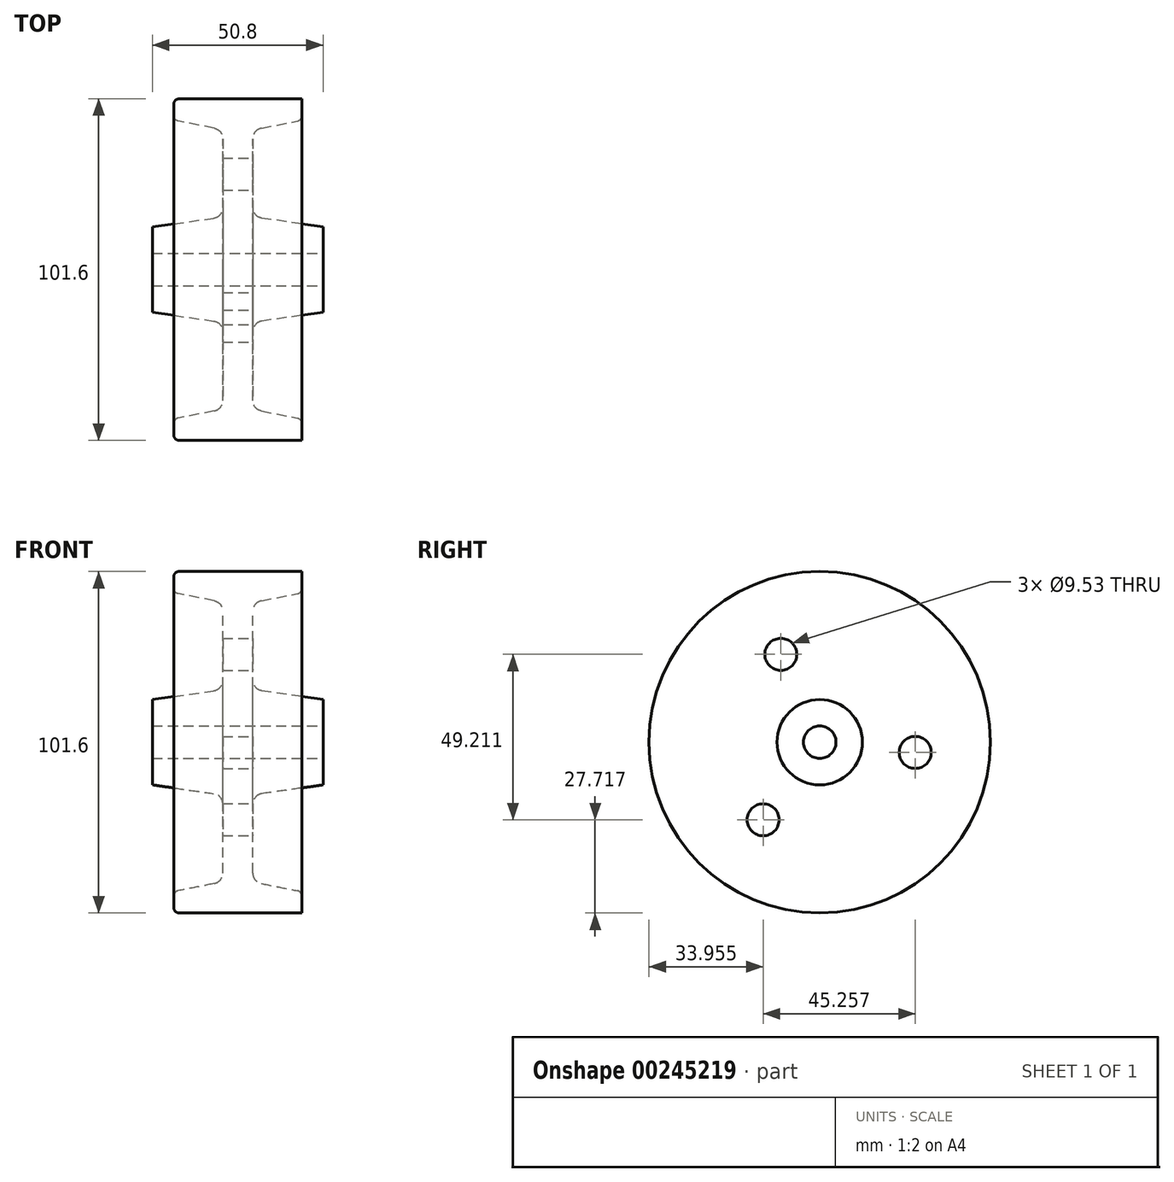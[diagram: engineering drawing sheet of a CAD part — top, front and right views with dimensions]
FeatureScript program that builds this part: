
annotation { "Feature Type Name" : "Feature", "Feature Type Description" : "" }
export const myFeature = defineFeature(function(context is Context, id is Id, definition is map)
    precondition{}
    {
        {
            var Q0;
            Q0=qCreatedBy(makeId("Front.planeOp"),FACE);
            var sketch = newSketch(context, id + "F0", { "sketchPlane" : qUnion([Q0])});
            skLineSegment(sketch, "E0", {"start": v(-43.53, 27.61) * mm, "end": v(7.27, 27.61) * mm});
            skLineSegment(sketch, "E1", {"start": v(7.27, 27.61) * mm, "end": v(7.27, 19.74) * mm});
            skLineSegment(sketch, "E2", {"start": v(-43.53, 27.61) * mm, "end": v(-43.53, 19.74) * mm});
            skLineSegment(sketch, "E3", {"start": v(-18.13, 27.61) * mm, "end": v(-18.13, -18.36) * mm});
            skLineSegment(sketch, "E4", {"start": v(-18.13, -18.36) * mm, "end": v(-35.59, -18.36) * mm});
            skLineSegment(sketch, "E5", {"start": v(-18.13, -18.36) * mm, "end": v(0.92, -18.36) * mm});
            skLineSegment(sketch, "E6", {"start": v(-37.18, -18.36) * mm, "end": v(-37.18, -12.01) * mm});
            skLineSegment(sketch, "E7", {"start": v(-37.18, -16.77) * mm, "end": v(-37.18, -13.31) * mm});
            skLineSegment(sketch, "E8", {"start": v(-25.13, -9.6) * mm, "end": v(-35.9, -11.76) * mm});
            skPoint(sketch, "E9.orphan", {"position": v(-37.18, -9.1) * mm});
            skLineSegment(sketch, "E10", {"start": v(-25.3, 17.14) * mm, "end": v(-43.53, 19.74) * mm});
            skLineSegment(sketch, "E11.MirrorCS", {"start": v(0.92, -16.77) * mm, "end": v(0.92, -13.31) * mm});
            skLineSegment(sketch, "E12.MirrorCS", {"start": v(-18.13, -18.36) * mm, "end": v(-0.66, -18.36) * mm});
            skLineSegment(sketch, "E13.MirrorCS", {"start": v(0.92, -18.36) * mm, "end": v(0.92, -12.01) * mm});
            skLineSegment(sketch, "E14.MirrorCS", {"start": v(-11.12, -9.6) * mm, "end": v(-0.35, -11.76) * mm});
            skLineSegment(sketch, "E15.MirrorCS", {"start": v(-10.95, 17.14) * mm, "end": v(7.27, 19.74) * mm});
            skPoint(sketch, "E16.MirrorP", {"position": v(0.92, -9.1) * mm});
            skPoint(sketch, "E17.end.orphan", {"position": v(-21.3, -10.7) * mm});
            skPoint(sketch, "E18.MirrorCS.end.orphan", {"position": v(-14.95, -6.4) * mm});
            skPoint(sketch, "E18.MirrorCS.start.orphan", {"position": v(-18.13, -5.1) * mm});
            skPoint(sketch, "E19.end.orphan", {"position": v(-21.3, -6.4) * mm});
            skPoint(sketch, "E20.MirrorCS.end.orphan", {"position": v(-14.95, -10.7) * mm});
            skPoint(sketch, "E21.orphan", {"position": v(-21.3, 27.61) * mm});
            skPoint(sketch, "E22.orphan", {"position": v(-14.95, 27.61) * mm});
            skLineSegment(sketch, "E23.trimOffspring", {"start": v(-22.58, -6.49) * mm, "end": v(-22.58, 14) * mm});
            skLineSegment(sketch, "E24.trimOffspring", {"start": v(-13.68, -6.49) * mm, "end": v(-13.68, 14) * mm});
            skPoint(sketch, "E25.MirrorCS.start.orphan", {"position": v(-14.95, -18.36) * mm});
            skPoint(sketch, "E26.start.orphan", {"position": v(-21.3, -18.36) * mm});
            skPoint(sketch, "E27.visualSharp", {"position": v(-22.58, -9.1) * mm});
            skArc(sketch, "E27.filletArc", {"start": v(-25.13, -9.6) * mm, "mid": v(-23.3, -8.5) * mm, "end": v(-22.58, -6.49) * mm});
            skPoint(sketch, "E28.visualSharp", {"position": v(-13.68, -9.1) * mm});
            skArc(sketch, "E28.filletArc", {"start": v(-13.68, -6.49) * mm, "mid": v(-12.96, -8.5) * mm, "end": v(-11.12, -9.6) * mm});
            skPoint(sketch, "E29.visualSharp", {"position": v(-22.58, 16.75) * mm});
            skArc(sketch, "E29.filletArc", {"start": v(-22.58, 14) * mm, "mid": v(-23.35, 16.07) * mm, "end": v(-25.3, 17.14) * mm});
            skPoint(sketch, "E30.visualSharp", {"position": v(-13.68, 16.75) * mm});
            skArc(sketch, "E30.filletArc", {"start": v(-10.95, 17.14) * mm, "mid": v(-12.9, 16.07) * mm, "end": v(-13.68, 14) * mm});
            skPoint(sketch, "E31.visualSharp", {"position": v(-37.18, -12.01) * mm});
            skArc(sketch, "E31.filletArc", {"start": v(-35.9, -11.76) * mm, "mid": v(-36.82, -12.3) * mm, "end": v(-37.18, -13.31) * mm});
            skPoint(sketch, "E32.visualSharp", {"position": v(0.92, -12.01) * mm});
            skArc(sketch, "E32.filletArc", {"start": v(0.92, -13.31) * mm, "mid": v(0.56, -12.3) * mm, "end": v(-0.35, -11.76) * mm});
            skPoint(sketch, "E33.visualSharp", {"position": v(0.92, -18.36) * mm});
            skArc(sketch, "E33.filletArc", {"start": v(-0.66, -18.36) * mm, "mid": v(0.46, -17.9) * mm, "end": v(0.92, -16.77) * mm});
            skPoint(sketch, "E34.visualSharp", {"position": v(-37.18, -18.36) * mm});
            skArc(sketch, "E34.filletArc", {"start": v(-37.18, -16.77) * mm, "mid": v(-36.71, -17.9) * mm, "end": v(-35.59, -18.36) * mm});
            skPoint(sketch, "E35.end.orphan", {"position": v(-18.13, 32.44) * mm});
            skLineSegment(sketch, "E36", {"start": v(9.17, 32.44) * mm, "end": v(-45.24, 32.44) * mm});
            skSolve(sketch);
        }
        {
            var Q0;
            {var subQ1=sQuery(id+"F0.wireOp",EDGE,"E2");Q0=makeQuery(id+"F0.imprint","IMPRINT",FACE,{"disambiguationData":[TD([[makeQuery(id+"F0.imprint","IMPRINT",EDGE,{"derivedFrom":subQ1}),1.0]])]});}
            var Q1;
            {var subQ4=sQuery(id+"F0.wireOp",EDGE,"E3");Q1=makeQuery(id+"F0.imprint","IMPRINT",FACE,{"disambiguationData":[TD([[makeQuery(id+"F0.imprint","IMPRINT",EDGE,{"derivedFrom":subQ4}),1.0]])]});}
            var Q2;
            {var subQ0=sQuery(id+"F0.wireOp",EDGE,"E5");Q2=makeQuery(id+"F0.imprint","IMPRINT",FACE,{"disambiguationData":[TD([[makeQuery(id+"F0.imprint","IMPRINT",EDGE,{"derivedFrom":subQ0}),1.0]])]});}
            var Q3;
            Q3=sQuery(id+"F0.wireOp",EDGE,"E36");
            revolve(context, id + "F1", {"entities" : qUnion([Q0, Q1, Q2]), "axis" : qUnion([Q3]), "revolveType" : RevolveType.FULL});
        }
        {
            var Q0;
            Q0=makeQuery(id+"F1.opRevolve","SWEPT_FACE",FACE,{"disambiguationData":[OSD([sQuery(id+"F0.wireOp",EDGE,"E1")])]});
            var sketch = newSketch(context, id + "F2", { "sketchPlane" : qUnion([Q0])});
            skLineSegment(sketch, "E37", {"start": v(0, 37.26) * mm, "end": v(0, 27.61) * mm});
            skLineSegment(sketch, "E38", {"start": v(0, 32.44) * mm, "end": v(4.83, 32.44) * mm});
            skLineSegment(sketch, "E39", {"start": v(0, 32.44) * mm, "end": v(-4.83, 32.44) * mm});
            skCircle(sketch, "E40", {"center": v(-11.57, 58.57) * mm, "radius": 4.76 * mm});
            skCircle(sketch, "E41", {"center": v(28.41, 29.4) * mm, "radius": 4.76 * mm});
            skCircle(sketch, "E42", {"center": v(-16.85, 9.36) * mm, "radius": 4.76 * mm});
            skSolve(sketch);
        }
        {
            var Q0;
            Q0=makeQuery(id+"F2.imprint","IMPRINT",FACE,{"disambiguationData":[TD([[makeQuery(id+"F2.imprint","IMPRINT",EDGE,{"derivedFrom":sQuery(id+"F2.wireOp",EDGE,"E40")}),1.0]])]});
            extrude(context, id + "F3", {"entities" : qUnion([Q0]), "operationType" : NewBodyOperationType.REMOVE, "oppositeDirection" : true, "depth" : 127 * mm});
        }
        {
            var Q0;
            Q0=makeQuery(id+"F2.imprint","IMPRINT",FACE,{"disambiguationData":[TD([[makeQuery(id+"F2.imprint","IMPRINT",EDGE,{"derivedFrom":sQuery(id+"F2.wireOp",EDGE,"E41")}),1.0]])]});
            var Q1;
            Q1=makeQuery(id+"F2.imprint","IMPRINT",FACE,{"disambiguationData":[TD([[makeQuery(id+"F2.imprint","IMPRINT",EDGE,{"derivedFrom":sQuery(id+"F2.wireOp",EDGE,"E42")}),1.0]])]});
            extrude(context, id + "F4", {"entities" : qUnion([Q0, Q1]), "operationType" : NewBodyOperationType.REMOVE, "oppositeDirection" : true, "depth" : 127 * mm});
        }
    });
